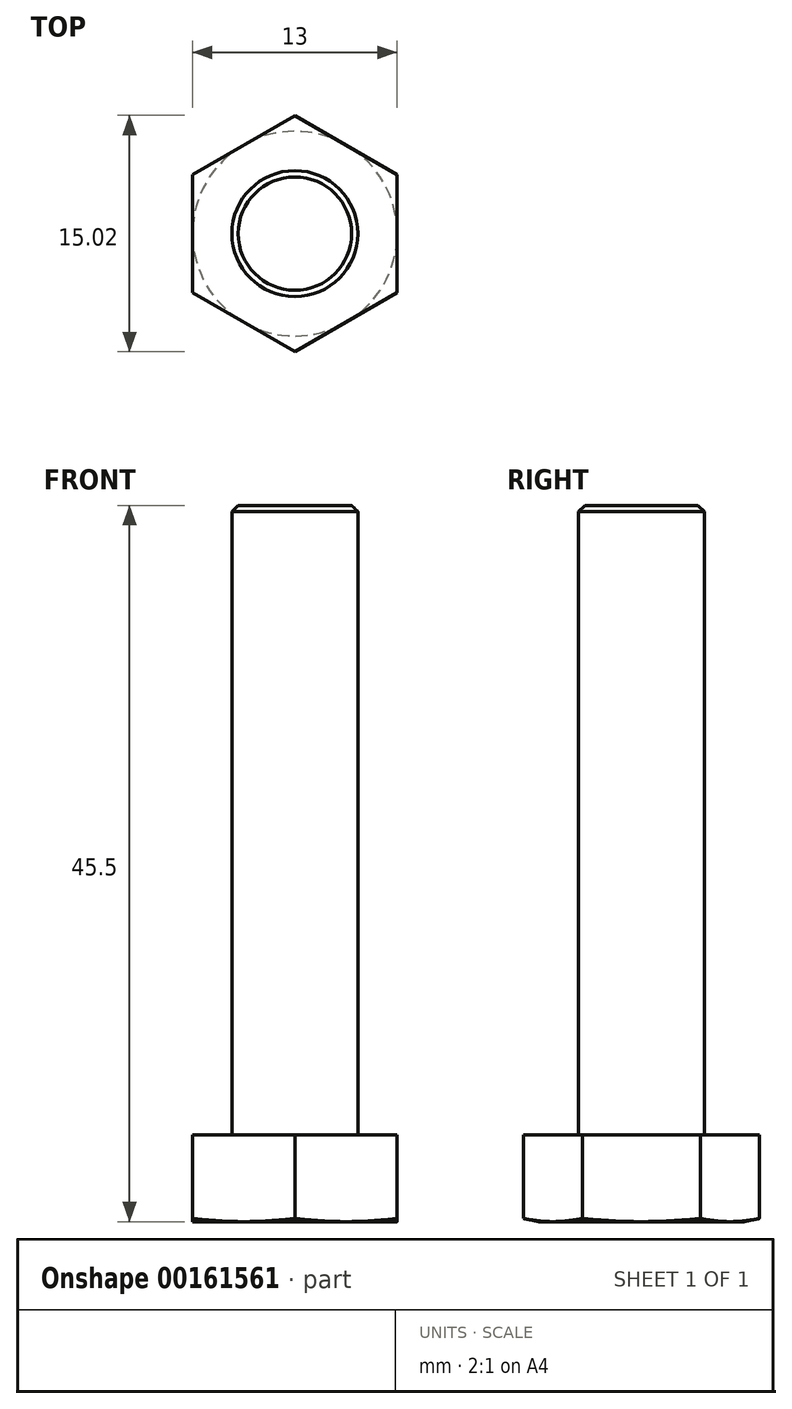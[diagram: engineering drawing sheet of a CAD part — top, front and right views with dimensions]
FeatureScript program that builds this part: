
annotation { "Feature Type Name" : "Feature", "Feature Type Description" : "" }
export const myFeature = defineFeature(function(context is Context, id is Id, definition is map)
    precondition{}
    {
        {
            var Q0;
            Q0=qCreatedBy(makeId("Top.planeOp"),FACE);
            var sketch = newSketch(context, id + "F0", { "sketchPlane" : qUnion([Q0])});
            skCircle(sketch, "E0.cCircle", {"center": v(0, 0) * mm, "radius": 6.5 * mm, "construction": true});
            skLineSegment(sketch, "E0.0", {"start": v(0, 7.5) * mm, "end": v(6.5, 3.75) * mm});
            skLineSegment(sketch, "E0.1", {"start": v(6.5, 3.75) * mm, "end": v(6.5, -3.75) * mm});
            skLineSegment(sketch, "E0.2", {"start": v(6.5, -3.75) * mm, "end": v(0, -7.5) * mm});
            skLineSegment(sketch, "E0.3", {"start": v(0, -7.5) * mm, "end": v(-6.5, -3.75) * mm});
            skLineSegment(sketch, "E0.4", {"start": v(-6.5, -3.75) * mm, "end": v(-6.5, 3.75) * mm});
            skLineSegment(sketch, "E0.5", {"start": v(-6.5, 3.75) * mm, "end": v(0, 7.5) * mm});
            skPoint(sketch, "E0.0.midPoint", {"position": v(3.25, 5.63) * mm});
            skSolve(sketch);
        }
        {
            var Q0;
            Q0=makeQuery(id+"F0.imprint","IMPRINT",FACE,{"disambiguationData":[TD([[makeQuery(id+"F0.imprint","IMPRINT",EDGE,{"derivedFrom":sQuery(id+"F0.wireOp",EDGE,"E0.0")}),-1.0]])]});
            extrude(context, id + "F1", {"entities" : qUnion([Q0]), "depth" : 5.5 * mm});
        }
        {
            var Q0;
            Q0=makeQuery(id+"F1.opExtrude","CAP_FACE",FACE,{"disambiguationData":[OSD([sQuery(id+"F0.wireOp",EDGE,"E0.0"),sQuery(id+"F0.wireOp",EDGE,"E0.1"),sQuery(id+"F0.wireOp",EDGE,"E0.2"),sQuery(id+"F0.wireOp",EDGE,"E0.3"),sQuery(id+"F0.wireOp",EDGE,"E0.4"),sQuery(id+"F0.wireOp",EDGE,"E0.5")])],"isStart":false});
            var sketch = newSketch(context, id + "F2", { "sketchPlane" : qUnion([Q0])});
            skCircle(sketch, "E1", {"center": v(0, 0) * mm, "radius": 4 * mm});
            skSolve(sketch);
        }
        {
            var Q0;
            Q0=makeQuery(id+"F2.imprint","IMPRINT",FACE,{"disambiguationData":[TD([[makeQuery(id+"F2.imprint","IMPRINT",EDGE,{"derivedFrom":sQuery(id+"F2.wireOp",EDGE,"E1")}),1.0]])]});
            extrude(context, id + "F3", {"entities" : qUnion([Q0]), "operationType" : NewBodyOperationType.ADD, "depth" : 40 * mm});
        }
        {
            var Q0;
            Q0=makeQuery(id+"F3.opExtrude","CAP_EDGE",EDGE,{"disambiguationData":[OSD([sQuery(id+"F2.wireOp",EDGE,"E1")])],"isStart":false});
            chamfer(context, id + "F4", {"entities" : qUnion([Q0]), "width" : 0.4 * mm, "tangentPropagation" : true});
        }
        {
            var Q0;
            Q0=qCreatedBy(makeId("Front.planeOp"),FACE);
            var sketch = newSketch(context, id + "F5", { "sketchPlane" : qUnion([Q0])});
            skLineSegment(sketch, "E2", {"start": v(-11.5, 0) * mm, "end": v(-6.5, 0) * mm});
            skLineSegment(sketch, "E3", {"start": v(-6.5, 0) * mm, "end": v(-11.5, 1) * mm});
            skLineSegment(sketch, "E4", {"start": v(-11.5, 1) * mm, "end": v(-11.5, 0) * mm});
            skSolve(sketch);
        }
        {
            var Q0;
            Q0 = qSketchRegion(id + "F5", true);
            var Q1;
            Q1=makeQuery(id+"F5.imprint","IMPRINT",FACE,{"disambiguationData":[TD([[makeQuery(id+"F5.imprint","IMPRINT",EDGE,{"derivedFrom":sQuery(id+"F5.wireOp",EDGE,"E2")}),1.0]])]});
            var Q2;
            Q2=makeQuery(id+"F3.opExtrude","SWEPT_FACE",FACE,{"disambiguationData":[OSD([sQuery(id+"F2.wireOp",EDGE,"E1")])]});
            revolve(context, id + "F6", {"operationType" : NewBodyOperationType.REMOVE, "entities" : qUnion([Q0, Q1]), "axis" : qUnion([Q2]), "revolveType" : RevolveType.FULL, "oppositeDirection" : true});
        }
    });
